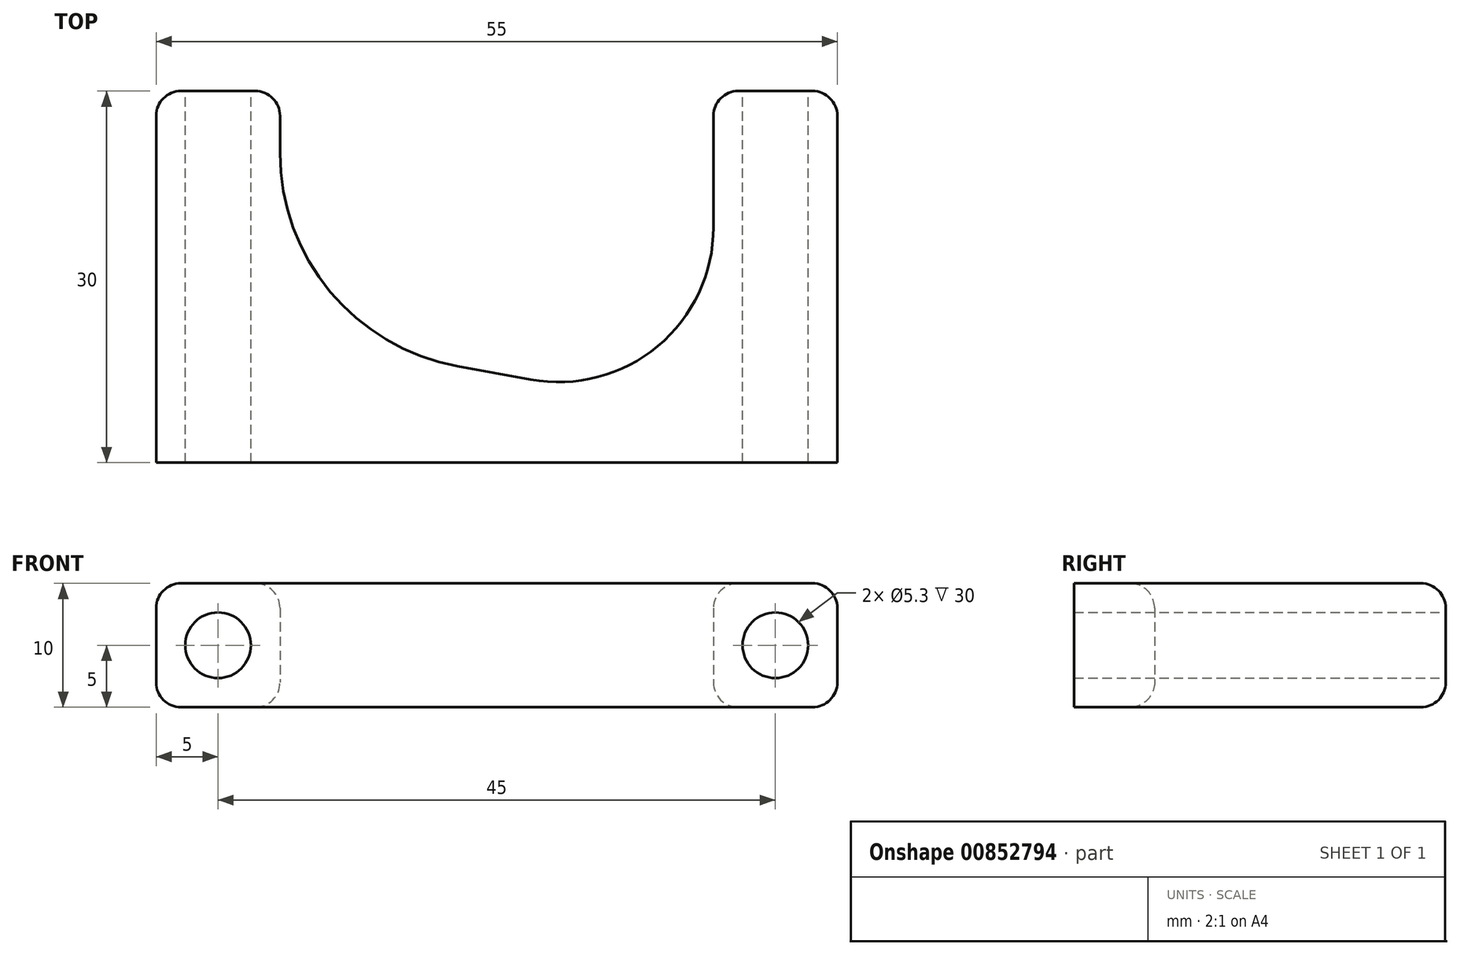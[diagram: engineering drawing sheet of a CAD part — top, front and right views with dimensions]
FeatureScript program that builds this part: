
annotation { "Feature Type Name" : "Feature", "Feature Type Description" : "" }
export const myFeature = defineFeature(function(context is Context, id is Id, definition is map)
    precondition{}
    {
        {
            var Q0;
            Q0=qCreatedBy(makeId("Top.planeOp"),FACE);
            var sketch = newSketch(context, id + "F0", { "sketchPlane" : qUnion([Q0])});
            skLineSegment(sketch, "E0", {"start": v(-10, 19) * mm, "end": v(-10, 30) * mm});
            skLineSegment(sketch, "E1", {"start": v(-10, 30) * mm, "end": v(0, 30) * mm});
            skLineSegment(sketch, "E2", {"start": v(0, 30) * mm, "end": v(0, 0) * mm});
            skLineSegment(sketch, "E3", {"start": v(-55, 0) * mm, "end": v(-55, 30) * mm});
            skLineSegment(sketch, "E4", {"start": v(-55, 30) * mm, "end": v(-45, 30) * mm});
            skLineSegment(sketch, "E5", {"start": v(-45, 30) * mm, "end": v(-10, 30) * mm, "construction": true});
            skLineSegment(sketch, "E6", {"start": v(-55, 0) * mm, "end": v(0, 0) * mm});
            skArc(sketch, "E7", {"start": v(-45, 25) * mm, "mid": v(-40.94, 13.8) * mm, "end": v(-30.66, 7.79) * mm});
            skLineSegment(sketch, "E8", {"start": v(-45, 30) * mm, "end": v(-45, 25) * mm});
            skArc(sketch, "E9", {"start": v(-24.75, 6.7) * mm, "mid": v(-14.5, 9.4) * mm, "end": v(-10, 19) * mm});
            skLineSegment(sketch, "E10", {"start": v(-30.66, 7.79) * mm, "end": v(-24.75, 6.7) * mm});
            skCircle(sketch, "E11", {"center": v(-35, 54.35) * mm, "radius": 17.5 * mm, "construction": true});
            skSolve(sketch);
        }
        {
            var Q0;
            Q0 = qSketchRegion(id + "F0", true);
            extrude(context, id + "F1", {"entities" : qUnion([Q0]), "depth" : 10 * mm, "offsetDistance" : 25 * mm});
        }
        {
            var Q0;
            Q0=makeQuery(id+"F1.opExtrude","SWEPT_FACE",FACE,{"disambiguationData":[OSD([sQuery(id+"F0.wireOp",EDGE,"E1")])]});
            var sketch = newSketch(context, id + "F2", { "sketchPlane" : qUnion([Q0])});
            skLineSegment(sketch, "E12", {"start": v(5, 0) * mm, "end": v(5, 10) * mm, "construction": true});
            skLineSegment(sketch, "E13", {"start": v(0, 5) * mm, "end": v(10, 5) * mm, "construction": true});
            skPoint(sketch, "E14", {"position": v(5, 5) * mm});
            skLineSegment(sketch, "E15.0", {"start": v(45, 10) * mm, "end": v(45, 0) * mm, "construction": true});
            skLineSegment(sketch, "E16.0", {"start": v(55, 10) * mm, "end": v(55, 0) * mm, "construction": true});
            skLineSegment(sketch, "E17", {"start": v(55, 5) * mm, "end": v(45, 5) * mm, "construction": true});
            skLineSegment(sketch, "E18", {"start": v(50, -5.3) * mm, "end": v(50, 17.76) * mm, "construction": true});
            skPoint(sketch, "E18.startSnap0", {"position": v(50, 5) * mm});
            skCircle(sketch, "E19", {"center": v(50, 5) * mm, "radius": 2.65 * mm});
            skCircle(sketch, "E20", {"center": v(5, 5) * mm, "radius": 2.65 * mm});
            skSolve(sketch);
        }
        {
            var Q0;
            Q0=makeQuery(id+"F2.imprint","IMPRINT",FACE,{"disambiguationData":[TD([[makeQuery(id+"F2.imprint","IMPRINT",EDGE,{"derivedFrom":sQuery(id+"F2.wireOp",EDGE,"E19")}),1.0]])]});
            extrude(context, id + "F3", {"entities" : qUnion([Q0]), "operationType" : NewBodyOperationType.REMOVE, "endBound" : BoundingType.THROUGH_ALL, "oppositeDirection" : true, "depth" : 25 * mm, "offsetDistance" : 25 * mm});
        }
        {
            var Q0;
            Q0=makeQuery(id+"F2.imprint","IMPRINT",FACE,{"disambiguationData":[TD([[makeQuery(id+"F2.imprint","IMPRINT",EDGE,{"derivedFrom":sQuery(id+"F2.wireOp",EDGE,"E20")}),1.0]])]});
            extrude(context, id + "F4", {"entities" : qUnion([Q0]), "operationType" : NewBodyOperationType.REMOVE, "endBound" : BoundingType.THROUGH_ALL, "oppositeDirection" : true, "depth" : 25 * mm, "offsetDistance" : 25 * mm});
        }
        {
            var Q0;
            Q0=makeQuery(id+"F1.opExtrude","CAP_EDGE",EDGE,{"disambiguationData":[OSD([sQuery(id+"F0.wireOp",EDGE,"E3")])],"isStart":false});
            var Q1;
            Q1=makeQuery(id+"F1.opExtrude","CAP_EDGE",EDGE,{"disambiguationData":[OSD([sQuery(id+"F0.wireOp",EDGE,"E2")])],"isStart":false});
            var Q2;
            Q2=makeQuery(id+"F1.opExtrude","CAP_EDGE",EDGE,{"disambiguationData":[OSD([sQuery(id+"F0.wireOp",EDGE,"E2")])],"isStart":true});
            var Q3;
            Q3=makeQuery(id+"F1.opExtrude","CAP_EDGE",EDGE,{"disambiguationData":[OSD([sQuery(id+"F0.wireOp",EDGE,"E3")])],"isStart":true});
            var Q4;
            Q4=makeQuery(id+"F1.opExtrude","CAP_EDGE",EDGE,{"disambiguationData":[OSD([sQuery(id+"F0.wireOp",EDGE,"E7")])],"isStart":true});
            var Q5;
            Q5=makeQuery(id+"F1.opExtrude","CAP_EDGE",EDGE,{"disambiguationData":[OSD([sQuery(id+"F0.wireOp",EDGE,"E9")])],"isStart":false});
            fillet(context, id + "F5", {"entities" : qUnion([Q0, Q1, Q2, Q3, Q4, Q5]), "radius" : 2 * mm, "tangentPropagation" : true, "allowEdgeOverflow" : false});
        }
        {
            var Q0;
            Q0=makeQuery(id+"F1.opExtrude","SWEPT_EDGE",EDGE,{"disambiguationData":[OSD([sQuery(id+"F0.wireOp",EDGE,"E0"),sQuery(id+"F0.wireOp",EDGE,"E1")])]});
            var Q1;
            Q1=makeQuery(id+"F1.opExtrude","SWEPT_EDGE",EDGE,{"disambiguationData":[OSD([sQuery(id+"F0.wireOp",EDGE,"E3"),sQuery(id+"F0.wireOp",EDGE,"E4")])]});
            fillet(context, id + "F6", {"entities" : qUnion([Q0, Q1]), "radius" : 2 * mm, "tangentPropagation" : true, "allowEdgeOverflow" : false});
        }
    });
